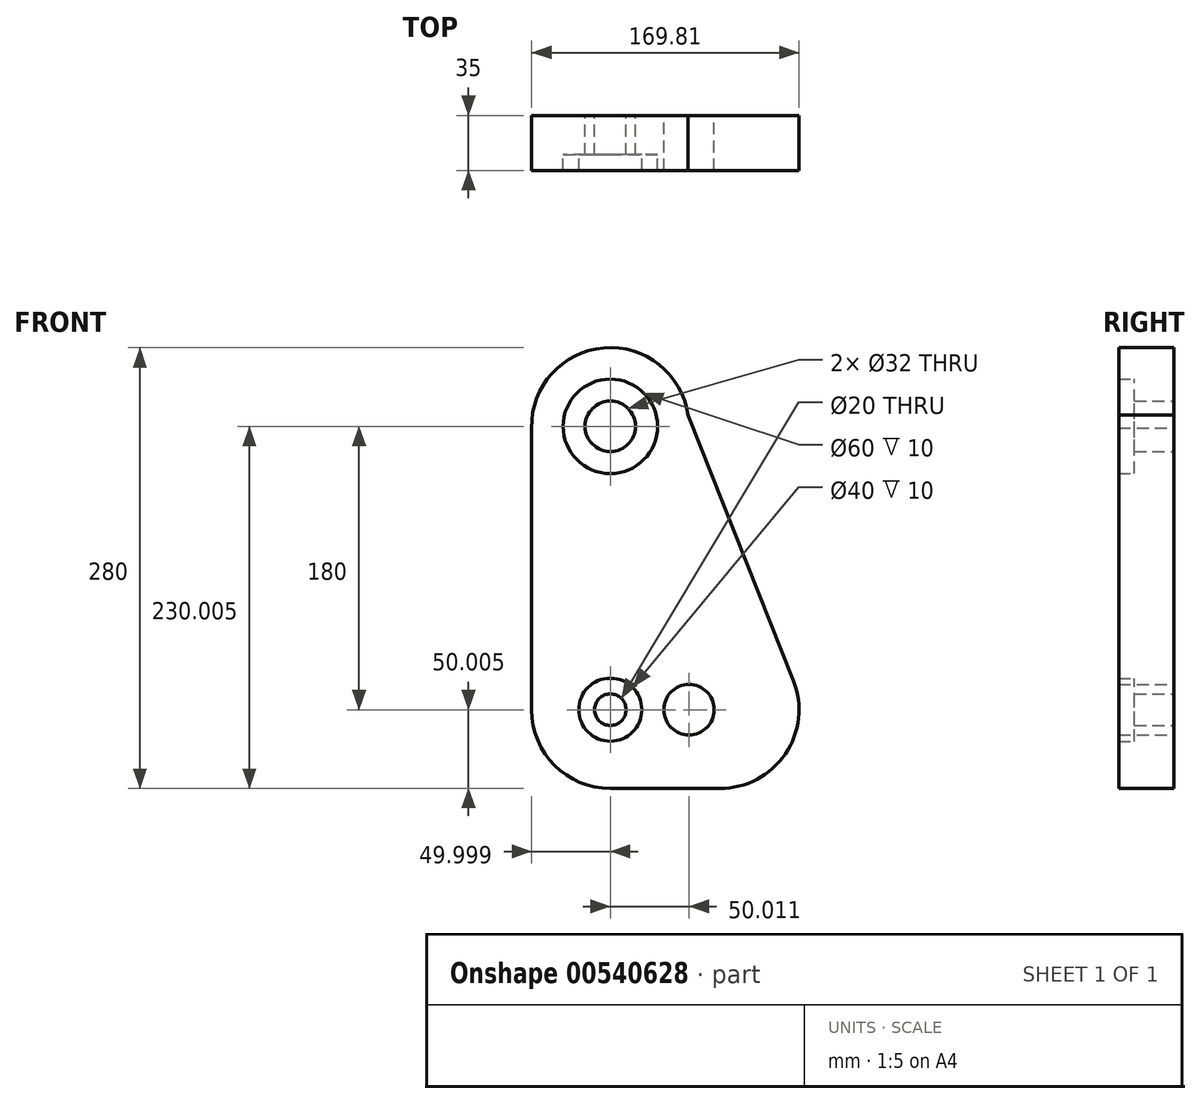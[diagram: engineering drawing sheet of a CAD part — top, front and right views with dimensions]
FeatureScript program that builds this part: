
annotation { "Feature Type Name" : "Feature", "Feature Type Description" : "" }
export const myFeature = defineFeature(function(context is Context, id is Id, definition is map)
    precondition{}
    {
        {
            var Q0;
            Q0=qCreatedBy(makeId("Front.planeOp"),FACE);
            var sketch = newSketch(context, id + "F0", { "sketchPlane" : qUnion([Q0])});
            skCircle(sketch, "E0", {"center": v(-36.25, -82.14) * mm, "radius": 20 * mm});
            skCircle(sketch, "E1", {"center": v(-36.25, -82.14) * mm, "radius": 10 * mm});
            skCircle(sketch, "E2", {"center": v(13.75, -82.14) * mm, "radius": 16 * mm});
            skArc(sketch, "E3", {"start": v(13.2, 105.2) * mm, "mid": v(-40.47, 147.69) * mm, "end": v(-86.25, 96.8) * mm});
            skCircle(sketch, "E4", {"center": v(-36.26, 97.86) * mm, "radius": 30 * mm});
            skCircle(sketch, "E5", {"center": v(-36.26, 97.86) * mm, "radius": 16 * mm});
            skLineSegment(sketch, "E6", {"start": v(-86.25, 98.94) * mm, "end": v(-86.25, -82.14) * mm});
            skLineSegment(sketch, "E7", {"start": v(-36.25, -132.14) * mm, "end": v(33.55, -132.14) * mm});
            skPoint(sketch, "E8.visualSharp", {"position": v(-86.25, -132.14) * mm});
            skArc(sketch, "E8.filletArc", {"start": v(-86.25, -82.14) * mm, "mid": v(-71.6, -117.5) * mm, "end": v(-36.25, -132.14) * mm});
            skLineSegment(sketch, "E9", {"start": v(80.04, -63.74) * mm, "end": v(13.2, 105.2) * mm});
            skPoint(sketch, "E10.visualSharp", {"position": v(107.1, -132.14) * mm});
            skArc(sketch, "E10.filletArc", {"start": v(33.55, -132.14) * mm, "mid": v(74.9, -110.24) * mm, "end": v(80.04, -63.74) * mm});
            skLineSegment(sketch, "E11", {"start": v(-36.25, 97.85) * mm, "end": v(-36.25, -82.14) * mm});
            skSolve(sketch);
        }
        {
            var Q0;
            Q0=makeQuery(id+"F0.imprint","IMPRINT",FACE,{"disambiguationData":[TD([[makeQuery(id+"F0.imprint","IMPRINT",EDGE,{"derivedFrom":sQuery(id+"F0.wireOp",EDGE,"E4")}),1.0]])]});
            var Q1;
            Q1=makeQuery(id+"F0.imprint","IMPRINT",FACE,{"disambiguationData":[TD([[makeQuery(id+"F0.imprint","IMPRINT",EDGE,{"derivedFrom":sQuery(id+"F0.wireOp",EDGE,"E0")}),1.0]])]});
            extrude(context, id + "F1", {"entities" : qUnion([Q0, Q1]), "depth" : 25 * mm, "offsetDistance" : 25 * mm});
        }
        {
            var Q0;
            Q0 = qSketchRegion(id + "F0", true);
            extrude(context, id + "F2", {"entities" : qUnion([Q0]), "operationType" : NewBodyOperationType.ADD, "depth" : 35 * mm, "offsetDistance" : 25 * mm});
        }
    });
